# Revit family: FA_ХомутЗаземленияЛенточный_EZETEK
name_source: partatom
category: Системы пожарной сигнализации
revit_build: Autodesk Revit 2017 (Build: 20160225_1515(x64)
units: mm (PartAtom-declared; Revit-internal decimal feet)

## family parameters
Всегда вертикально = Да
На основе рабочей плоскости = Нет
Общий = Да
При загрузке вырезать с полостями = Нет
Размер круглого соединителя = Использовать радиус
Сохранять ориентацию аннотаций = Нет
Тип детали = Нормальный
Точка расчета площади = Нет

## types (5) — shared parameters
ADSK_Версия Revit = 2017
ADSK_Единица измерения = шт.
ADSK_Завод-изготовитель = Ezetek
ADSK_Количество = 1
URL = https://ezetek.ru
Группа модели = Держатели и хомуты
Изготовитель = Ezetek
Описание = Хомут заземления применяется для подключения металлических труб в систему уравнивания потенциалов. Провод заземления подключает к хомуту при помощи болта c резьбой М6.
Угол = 90.00°

## per-type parameters (varying)
| type | ADSK_Код изделия | ADSK_Марка | ADSK_Масса | ADSK_Масса_Текст | ADSK_Материал | ADSK_Наименование | ADSK_Обозначение |
| ХомутЗаземленияЛенточный_91320-1 | 91320-1 | 91320-1 | 0.051 | 0.051 | BIMLIB_Сталь_Нержавеющая_EZETEK | Хомут ленточный 5-25 мм, нерж | 91320-1 |
| ХомутЗаземленияЛенточный_91326-1 | 91326-1 | 91326-1 | 0.054 | 0.054 | BIMLIB_Сталь_Нержавеющая_EZETEK | Хомут ленточный 20-50 мм, нерж | 91326-1 |
| ХомутЗаземленияЛенточный_91321 | 91321 | 91321 | 0.052 | 0.052 | BIMLIB_Медь_Никелированная_EZETEK | Хомут ленточный 20-48 мм, медь никелированная | 91321 |
| ХомутЗаземленияЛенточный_91322 | 91322 | 91322 | 0.062 | 0.062 | BIMLIB_Медь_Никелированная_EZETEK | Хомут ленточный 20-115 мм, медь никелированная | 91322 |
| ХомутЗаземленияЛенточный_91323 | 91323 | 91323 | 0.071 | 0.071 | BIMLIB_Медь_Никелированная_EZETEK | Хомут ленточный 20-165 мм, медь никелированная | 91323 |
